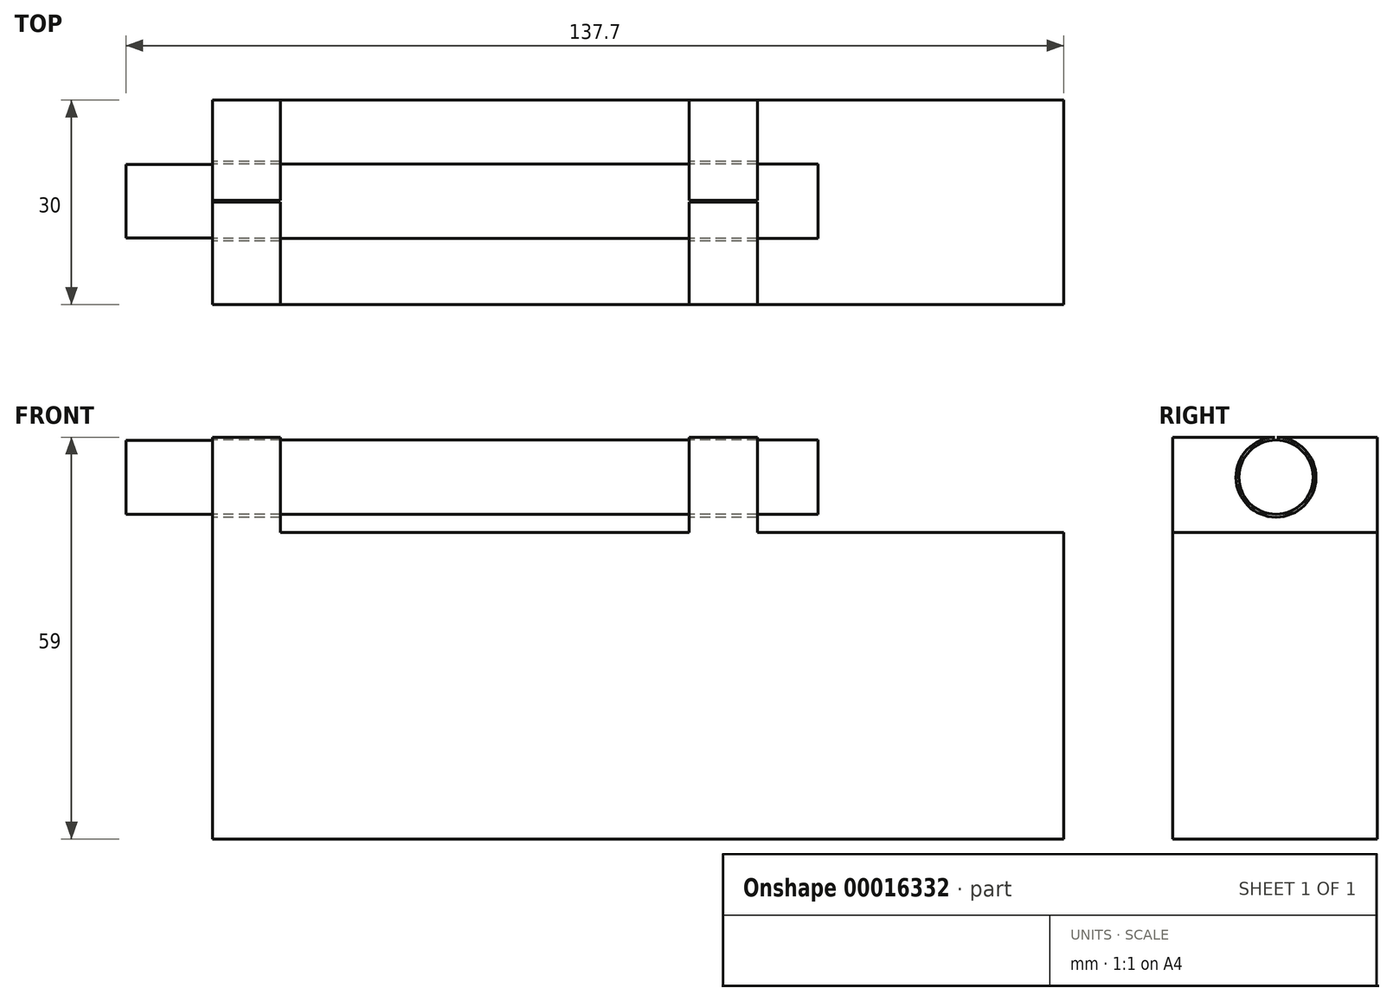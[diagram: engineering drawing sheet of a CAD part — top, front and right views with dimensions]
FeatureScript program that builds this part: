
annotation { "Feature Type Name" : "Feature", "Feature Type Description" : "" }
export const myFeature = defineFeature(function(context is Context, id is Id, definition is map)
    precondition{}
    {
        {
            var Q0;
            Q0=qCreatedBy(makeId("Top.planeOp"),FACE);
            var sketch = newSketch(context, id + "F0", { "sketchPlane" : qUnion([Q0])});
            skLineSegment(sketch, "E0.rect.bottom", {"start": v(62.5, 15) * mm, "end": v(-62.5, 15) * mm});
            skLineSegment(sketch, "E0.rect.top", {"start": v(62.5, -15) * mm, "end": v(-62.5, -15) * mm});
            skLineSegment(sketch, "E0.rect.left", {"start": v(62.5, 15) * mm, "end": v(62.5, -15) * mm});
            skLineSegment(sketch, "E0.rect.right", {"start": v(-62.5, 15) * mm, "end": v(-62.5, -15) * mm});
            skPoint(sketch, "E0.rect.middle", {"position": v(0, 0) * mm});
            skSolve(sketch);
        }
        {
            var Q0;
            Q0 = qSketchRegion(id + "F0", true);
            extrude(context, id + "F1", {"entities" : qUnion([Q0]), "depth" : 45 * mm});
        }
        {
            var Q0;
            Q0=makeQuery(id+"F1.opExtrude","CAP_FACE",FACE,{"disambiguationData":[OSD([sQuery(id+"F0.wireOp",EDGE,"E0.rect.bottom"),sQuery(id+"F0.wireOp",EDGE,"E0.rect.top"),sQuery(id+"F0.wireOp",EDGE,"E0.rect.left"),sQuery(id+"F0.wireOp",EDGE,"E0.rect.right")])],"isStart":false});
            var sketch = newSketch(context, id + "F2", { "sketchPlane" : qUnion([Q0])});
            skLineSegment(sketch, "E1.bottom", {"start": v(-62.5, 15) * mm, "end": v(17.5, 15) * mm});
            skLineSegment(sketch, "E1.top", {"start": v(-62.5, -15) * mm, "end": v(17.5, -15) * mm});
            skLineSegment(sketch, "E1.left", {"start": v(-62.5, 15) * mm, "end": v(-62.5, -15) * mm});
            skLineSegment(sketch, "E1.right", {"start": v(17.5, 15) * mm, "end": v(17.5, -15) * mm});
            skSolve(sketch);
        }
        {
            var Q0;
            Q0 = qSketchRegion(id + "F2", true);
            extrude(context, id + "F3", {"entities" : qUnion([Q0]), "operationType" : NewBodyOperationType.ADD, "depth" : 14 * mm});
        }
        {
            var Q0;
            Q0=makeQuery(id+"F3.opExtrude","CAP_FACE",FACE,{"disambiguationData":[OSD([sQuery(id+"F2.wireOp",EDGE,"E1.bottom"),sQuery(id+"F2.wireOp",EDGE,"E1.top"),sQuery(id+"F2.wireOp",EDGE,"E1.left"),sQuery(id+"F2.wireOp",EDGE,"E1.right")])],"isStart":false});
            var sketch = newSketch(context, id + "F4", { "sketchPlane" : qUnion([Q0])});
            skLineSegment(sketch, "E2.bottom", {"start": v(-52.5, 15) * mm, "end": v(7.5, 15) * mm});
            skLineSegment(sketch, "E2.top", {"start": v(-52.5, -15) * mm, "end": v(7.5, -15) * mm});
            skLineSegment(sketch, "E2.left", {"start": v(-52.5, 15) * mm, "end": v(-52.5, -15) * mm});
            skLineSegment(sketch, "E2.right", {"start": v(7.5, 15) * mm, "end": v(7.5, -15) * mm});
            skSolve(sketch);
        }
        {
            var Q0;
            Q0 = qSketchRegion(id + "F4", true);
            extrude(context, id + "F5", {"entities" : qUnion([Q0]), "operationType" : NewBodyOperationType.REMOVE, "oppositeDirection" : true, "depth" : 14 * mm});
        }
        {
            var Q0;
            Q0=makeQuery(id+"F3.boolean.opBoolean","MERGE",FACE,{"derivedFrom":[makeQuery(id+"F1.opExtrude","SWEPT_FACE",FACE,{"disambiguationData":[OSD([sQuery(id+"F0.wireOp",EDGE,"E0.rect.right")])]}),makeQuery(id+"F3.opExtrude","SWEPT_FACE",FACE,{"disambiguationData":[OSD([sQuery(id+"F2.wireOp",EDGE,"E1.left")])]})]});
            var sketch = newSketch(context, id + "F6", { "sketchPlane" : qUnion([Q0])});
            skLineSegment(sketch, "E3", {"start": v(-15, 59) * mm, "end": v(15, 59) * mm, "construction": true});
            skCircle(sketch, "E4", {"center": v(-0.15, 53.13) * mm, "radius": 5.87 * mm});
            skPoint(sketch, "E4.first.point", {"position": v(0, 59) * mm});
            skPoint(sketch, "E4.second.point", {"position": v(0, 47.27) * mm});
            skPoint(sketch, "E4.third.point", {"position": v(-6.02, 53.07) * mm});
            skSolve(sketch);
        }
        {
            var Q0;
            Q0 = qSketchRegion(id + "F6", true);
            var Q1;
            Q1=makeQuery(id+"F3.opExtrude","SWEPT_FACE",FACE,{"disambiguationData":[OSD([sQuery(id+"F2.wireOp",EDGE,"E1.right")])]});
            extrude(context, id + "F7", {"entities" : qUnion([Q0]), "operationType" : NewBodyOperationType.REMOVE, "endBound" : BoundingType.UP_TO_SURFACE, "oppositeDirection" : true, "endBoundEntityFace" : qUnion([Q1]), "depth" : 25.4 * mm});
        }
        {
            var Q0;
            Q0=makeQuery(id+"F3.boolean.opBoolean","MERGE",FACE,{"derivedFrom":[makeQuery(id+"F1.opExtrude","SWEPT_FACE",FACE,{"disambiguationData":[OSD([sQuery(id+"F0.wireOp",EDGE,"E0.rect.right")])]}),makeQuery(id+"F3.opExtrude","SWEPT_FACE",FACE,{"disambiguationData":[OSD([sQuery(id+"F2.wireOp",EDGE,"E1.left")])]})]});
            var sketch = newSketch(context, id + "F8", { "sketchPlane" : qUnion([Q0])});
            skCircle(sketch, "E5", {"center": v(-0.15, 53.13) * mm, "radius": 5.42 * mm});
            skSolve(sketch);
        }
        {
            var Q0;
            Q0 = qSketchRegion(id + "F8", true);
            extrude(context, id + "F9", {"entities" : qUnion([Q0]), "depth" : 12.7 * mm});
        }
        {
            var Q0;
            Q0=makeQuery(id+"F9.opExtrude","CAP_FACE",FACE,{"disambiguationData":[OSD([sQuery(id+"F8.wireOp",EDGE,"E5")])],"isStart":true});
            var sketch = newSketch(context, id + "F10", { "sketchPlane" : qUnion([Q0])});
            skCircle(sketch, "E6", {"center": v(0.15, 53.13) * mm, "radius": 5.44 * mm});
            skSolve(sketch);
        }
        {
            var Q0;
            Q0 = qSketchRegion(id + "F10", true);
            extrude(context, id + "F11", {"entities" : qUnion([Q0]), "operationType" : NewBodyOperationType.ADD, "depth" : 88.9 * mm});
        }
    });
